# Revit family: Hager-VECTOR-Surface_mounted-IP65-With_Cover-With_DIN-NoHosted-CH-de
name_source: partatom
category: Electrical Equipment
units: mm (PartAtom-declared; Revit-internal decimal feet)

## family parameters
Always vertical = Yes
Cut with Voids When Loaded = No
Maintain Annotation Orientation = No
Panel Configuration = Two Columns, Circuits Across
Part Type = Panelboard
Room Calculation Point = No
Round Connector Dimension = Use Diameter
Shared = No
Work Plane-Based = Yes

## types (30) — shared parameters
Code hager = ADD-EC000214_EU
Default Elevation = 1200 mm
EF000003 - Montageart = Aufputz
EF000007 - Farbe = grau
EF000024 - UV-beständig = No
EF000116 - RAL-Nummer = 7035
EF000118 - Mit Montageplatte = No
EF001062 - EMV-Ausführung = No
EF001088 - Anbaumöglichkeit = Yes
EF001134 - DIN-Schiene = Yes
EF004462 - Art der Schließung = sonstige
EF005474 - Schutzart (IP) = IP65
EF006244 - Transparenter Deckel/Tür = Yes
EF006306 - Mit Schloss = No
EF015941 - Signaldurchlassende Tür = Yes
ETIM class code = EC000214
ETIM class name = Small distribution board
HG000001-Anzahl der Spalten = 1
HG000002-Mit tür = Yes
HG000003-Bereich = VECTOR
HG000005-Dicke = 2 mm  [stored 0.00656168 ft]
HG000006-Flush mounted = No
HG000009-Doppelflügeligen Tür = No
HG000010-Asymmetrische Türen = No
HG000011-Leere Reihen von unten = No
HG000012-Türschwenkwinkel = 90.00°
HG000013-Tür links = No
HG000014-Tür rechts = Yes
HG000015-Sichtbarkeit der Türöffnung = Yes
HG000016-3D-Türsichtbarkeit = Yes
HG000017-Distanz zwischen den Polen = 18 mm  [stored 0.0590551 ft]
HG000060-RAL-number = 7035
HG000099-Onfly Template ID-de-DE = 507532
Manufacturer = Hager
Name BIM&CO = Electricity
Name hager = ADD_Enclosures_EC000214
Reference = Template-Enclosure_EU-EC000214
Uniformat = Low Tension Service & Dist.
Uniformat code = D501001
zero-valued in all types: EF000218 - Einbautiefe, EF000332 - Einbauhöhe, EF000846 - Einbaubreite, EF001131 - Innentiefe, HG000007-Anzahl der leeren Spalten, HG000008-Anzahl der leeren Reihen

## per-type parameters (varying)
| type | BC_METADATA | EF000008 - Breite | EF000040 - Höhe | EF000049 - Tiefe | EF000266 - Anzahl der Reihen | EF002950 - Breite in Teilungseinheiten | EF009212 - Ausführung Deckel | EF015776 - Erdungsklemmenblock | EF015777 - Neutralleiterklemmenblock | HG000004-Herstellerreferenz | HGEF000266-Anzahl der Reihen | HGEF0002950-Breite in Teilungseinheiten |
| VECTOR-Surface_mounted_W111_H175_D93_3_Modular_Spacing-VE103A | {"ObjectGuid":"d3c7cbe9-06a7-4916-a6f3-f6102e421bbc","ModelGuid":"fb386d16-bb01-46b0-871a-5d369bb861f8","VariantGuid":"69505e22-49fc-412b-8c65-e0a7629c260b","Revision":"#30","VariantName":"VECTOR-Surface_mounted_W111_H175_D93_3_Modular_Spacing-VE103A"} | 111 mm | 175 mm  [stored 0.574147 ft] | 93 mm  [stored 0.305118 ft] | 1 | 3 | geschlossen | Yes | No | VE103A | 1 | 3 |
| VECTOR-Surface_mounted_W111_H175_D93_3_Modular_Spacing-VE103PN | {"ObjectGuid":"d3c7cbe9-06a7-4916-a6f3-f6102e421bbc","ModelGuid":"fb386d16-bb01-46b0-871a-5d369bb861f8","VariantGuid":"5bf82279-769e-45e9-843e-734a2e8b04b2","Revision":"#30","VariantName":"VECTOR-Surface_mounted_W111_H175_D93_3_Modular_Spacing-VE103PN"} | 111 mm | 175 mm  [stored 0.574147 ft] | 93 mm  [stored 0.305118 ft] | 1 | 3 | mit Ausschnitt | No | No | VE103PN | 1 | 3 |
| VECTOR-Surface_mounted_W111_H175_D93_3_Modular_Spacing-VE103SN | {"ObjectGuid":"d3c7cbe9-06a7-4916-a6f3-f6102e421bbc","ModelGuid":"fb386d16-bb01-46b0-871a-5d369bb861f8","VariantGuid":"e7d898c2-087d-478f-bfbd-9c783f3fbaf0","Revision":"#30","VariantName":"VECTOR-Surface_mounted_W111_H175_D93_3_Modular_Spacing-VE103SN"} | 111 mm | 175 mm  [stored 0.574147 ft] | 93 mm  [stored 0.305118 ft] | 1 | 3 | mit Ausschnitt | No | No | VE103SN | 1 | 3 |
| VECTOR-Surface_mounted_W165_H190_D113_6_Modular_Spacing-VE106A | {"ObjectGuid":"d3c7cbe9-06a7-4916-a6f3-f6102e421bbc","ModelGuid":"fb386d16-bb01-46b0-871a-5d369bb861f8","VariantGuid":"e3f62185-71a5-4f86-a256-2cf27b2b70b2","Revision":"#30","VariantName":"VECTOR-Surface_mounted_W165_H190_D113_6_Modular_Spacing-VE106A"} | 165 mm | 190 mm | 113 mm  [stored 0.370735 ft] | 1 | 6 | geschlossen | Yes | No | VE106A | 1 | 6 |
| VECTOR-Surface_mounted_W165_H190_D113_6_Modular_Spacing-VE106PN | {"ObjectGuid":"d3c7cbe9-06a7-4916-a6f3-f6102e421bbc","ModelGuid":"fb386d16-bb01-46b0-871a-5d369bb861f8","VariantGuid":"76445b86-cd2d-4a67-a9fa-ffff4e2ed3c8","Revision":"#30","VariantName":"VECTOR-Surface_mounted_W165_H190_D113_6_Modular_Spacing-VE106PN"} | 165 mm | 190 mm | 113 mm  [stored 0.370735 ft] | 1 | 6 | geschlossen | No | No | VE106PN | 1 | 6 |
| VECTOR-Surface_mounted_W165_H190_D113_6_Modular_Spacing-VE106SN | {"ObjectGuid":"d3c7cbe9-06a7-4916-a6f3-f6102e421bbc","ModelGuid":"fb386d16-bb01-46b0-871a-5d369bb861f8","VariantGuid":"b0e8016f-7a6b-4585-a6ec-a9ff9729da40","Revision":"#30","VariantName":"VECTOR-Surface_mounted_W165_H190_D113_6_Modular_Spacing-VE106SN"} | 165 mm | 190 mm | 113 mm  [stored 0.370735 ft] | 1 | 6 | mit Ausschnitt | No | No | VE106SN | 1 | 6 |
| VECTOR-Surface_mounted_W237_H210_D114_10_Modular_Spacing-VE110A | {"ObjectGuid":"d3c7cbe9-06a7-4916-a6f3-f6102e421bbc","ModelGuid":"fb386d16-bb01-46b0-871a-5d369bb861f8","VariantGuid":"4d85095b-6905-44da-a693-27a8f614f5e6","Revision":"#30","VariantName":"VECTOR-Surface_mounted_W237_H210_D114_10_Modular_Spacing-VE110A"} | 237 mm  [stored 0.777559 ft] | 210 mm  [stored 0.688976 ft] | 114 mm  [stored 0.374016 ft] | 1 | 10 | geschlossen | Yes | No | VE110A | 1 | 10 |
| VECTOR-Surface_mounted_W237_H210_D114_10_Modular_Spacing-VE110PN | {"ObjectGuid":"d3c7cbe9-06a7-4916-a6f3-f6102e421bbc","ModelGuid":"fb386d16-bb01-46b0-871a-5d369bb861f8","VariantGuid":"8b8af41c-55d3-4f54-a48d-69fb1ebbe829","Revision":"#30","VariantName":"VECTOR-Surface_mounted_W237_H210_D114_10_Modular_Spacing-VE110PN"} | 237 mm  [stored 0.777559 ft] | 210 mm  [stored 0.688976 ft] | 114 mm  [stored 0.374016 ft] | 1 | 10 | geschlossen | No | No | VE110PN | 1 | 10 |
| VECTOR-Surface_mounted_W237_H210_D114_10_Modular_Spacing-VE110SN | {"ObjectGuid":"d3c7cbe9-06a7-4916-a6f3-f6102e421bbc","ModelGuid":"fb386d16-bb01-46b0-871a-5d369bb861f8","VariantGuid":"02d3d4a0-a31d-4200-83ef-eeb133a9bbc4","Revision":"#30","VariantName":"VECTOR-Surface_mounted_W237_H210_D114_10_Modular_Spacing-VE110SN"} | 237 mm  [stored 0.777559 ft] | 210 mm  [stored 0.688976 ft] | 114 mm  [stored 0.374016 ft] | 1 | 10 | geschlossen | No | No | VE110SN | 1 | 10 |
| VECTOR-Surface_mounted_W310_H302_D151_12_Modular_Spacing-VE112AK | {"ObjectGuid":"d3c7cbe9-06a7-4916-a6f3-f6102e421bbc","ModelGuid":"fb386d16-bb01-46b0-871a-5d369bb861f8","VariantGuid":"d57e2aae-6186-4f79-9daa-0f27d3ef683b","Revision":"#30","VariantName":"VECTOR-Surface_mounted_W310_H302_D151_12_Modular_Spacing-VE112AK"} | 310 mm  [stored 1.01706 ft] | 302 mm  [stored 0.990814 ft] | 151 mm  [stored 0.495407 ft] | 1 | 12 | geschlossen | Yes | Yes | VE112AK | 1 | 12 |
| VECTOR-Surface_mounted_W310_H302_D151_12_Modular_Spacing-VE112PN | {"ObjectGuid":"d3c7cbe9-06a7-4916-a6f3-f6102e421bbc","ModelGuid":"fb386d16-bb01-46b0-871a-5d369bb861f8","VariantGuid":"1bbf5467-8e35-420d-9748-48cfdb1c49db","Revision":"#30","VariantName":"VECTOR-Surface_mounted_W310_H302_D151_12_Modular_Spacing-VE112PN"} | 310 mm  [stored 1.01706 ft] | 302 mm  [stored 0.990814 ft] | 151 mm  [stored 0.495407 ft] | 1 | 12 | geschlossen | No | No | VE112PN | 1 | 12 |
| VECTOR-Surface_mounted_W310_H302_D151_12_Modular_Spacing-VE112SN | {"ObjectGuid":"d3c7cbe9-06a7-4916-a6f3-f6102e421bbc","ModelGuid":"fb386d16-bb01-46b0-871a-5d369bb861f8","VariantGuid":"2669eab4-d3bd-4278-87ef-f939ce0a811b","Revision":"#30","VariantName":"VECTOR-Surface_mounted_W310_H302_D151_12_Modular_Spacing-VE112SN"} | 310 mm  [stored 1.01706 ft] | 302 mm  [stored 0.990814 ft] | 151 mm  [stored 0.495407 ft] | 1 | 12 | geschlossen | No | No | VE112SN | 1 | 12 |
| VECTOR-Surface_mounted_W418_H302_D151_18_Modular_Spacing-VE118AK | {"ObjectGuid":"d3c7cbe9-06a7-4916-a6f3-f6102e421bbc","ModelGuid":"fb386d16-bb01-46b0-871a-5d369bb861f8","VariantGuid":"f4e0934a-e4f0-446a-89c8-3abac548046a","Revision":"#30","VariantName":"VECTOR-Surface_mounted_W418_H302_D151_18_Modular_Spacing-VE118AK"} | 418 mm  [stored 1.37139 ft] | 302 mm  [stored 0.990814 ft] | 151 mm  [stored 0.495407 ft] | 1 | 18 | geschlossen | Yes | Yes | VE118AK | 1 | 18 |
| VECTOR-Surface_mounted_W418_H302_D151_18_Modular_Spacing-VE118PN | {"ObjectGuid":"d3c7cbe9-06a7-4916-a6f3-f6102e421bbc","ModelGuid":"fb386d16-bb01-46b0-871a-5d369bb861f8","VariantGuid":"06ed9296-9994-441a-a687-3948c0a79dd1","Revision":"#30","VariantName":"VECTOR-Surface_mounted_W418_H302_D151_18_Modular_Spacing-VE118PN"} | 418 mm  [stored 1.37139 ft] | 302 mm  [stored 0.990814 ft] | 151 mm  [stored 0.495407 ft] | 1 | 18 | geschlossen | No | No | VE118PN | 1 | 18 |
| VECTOR-Surface_mounted_W418_H302_D151_18_Modular_Spacing-VE118SN | {"ObjectGuid":"d3c7cbe9-06a7-4916-a6f3-f6102e421bbc","ModelGuid":"fb386d16-bb01-46b0-871a-5d369bb861f8","VariantGuid":"4a2194d9-89a4-4a4b-ac45-6e89e3566a8e","Revision":"#30","VariantName":"VECTOR-Surface_mounted_W418_H302_D151_18_Modular_Spacing-VE118SN"} | 418 mm  [stored 1.37139 ft] | 302 mm  [stored 0.990814 ft] | 151 mm  [stored 0.495407 ft] | 1 | 18 | geschlossen | No | No | VE118SN | 1 | 18 |
| VECTOR-Surface_mounted_W310_H427_D151_12_Modular_Spacing-VE212AK | {"ObjectGuid":"d3c7cbe9-06a7-4916-a6f3-f6102e421bbc","ModelGuid":"fb386d16-bb01-46b0-871a-5d369bb861f8","VariantGuid":"c01b0445-b96e-4ca0-8f36-f3b77660627c","Revision":"#30","VariantName":"VECTOR-Surface_mounted_W310_H427_D151_12_Modular_Spacing-VE212AK"} | 310 mm  [stored 1.01706 ft] | 427 mm  [stored 1.40092 ft] | 151 mm  [stored 0.495407 ft] | 2 | 12 | geschlossen | Yes | Yes | VE212AK | 2 | 12 |
| VECTOR-Surface_mounted_W310_H427_D151_12_Modular_Spacing-VE212PN | {"ObjectGuid":"d3c7cbe9-06a7-4916-a6f3-f6102e421bbc","ModelGuid":"fb386d16-bb01-46b0-871a-5d369bb861f8","VariantGuid":"29390155-c559-412c-8a29-67b206487e47","Revision":"#30","VariantName":"VECTOR-Surface_mounted_W310_H427_D151_12_Modular_Spacing-VE212PN"} | 310 mm  [stored 1.01706 ft] | 427 mm  [stored 1.40092 ft] | 151 mm  [stored 0.495407 ft] | 2 | 12 | geschlossen | No | No | VE212PN | 2 | 12 |
| VECTOR-Surface_mounted_W310_H427_D151_12_Modular_Spacing-VE212SN | {"ObjectGuid":"d3c7cbe9-06a7-4916-a6f3-f6102e421bbc","ModelGuid":"fb386d16-bb01-46b0-871a-5d369bb861f8","VariantGuid":"e55af2bb-5e56-47f6-8731-15f48f08de25","Revision":"#30","VariantName":"VECTOR-Surface_mounted_W310_H427_D151_12_Modular_Spacing-VE212SN"} | 310 mm  [stored 1.01706 ft] | 427 mm  [stored 1.40092 ft] | 151 mm  [stored 0.495407 ft] | 2 | 12 | geschlossen | No | No | VE212SN | 2 | 12 |
| VECTOR-Surface_mounted_W418_H452_D151_18_Modular_Spacing-VE218AK | {"ObjectGuid":"d3c7cbe9-06a7-4916-a6f3-f6102e421bbc","ModelGuid":"fb386d16-bb01-46b0-871a-5d369bb861f8","VariantGuid":"071168f8-5f04-42d3-9594-f27b45a714b0","Revision":"#30","VariantName":"VECTOR-Surface_mounted_W418_H452_D151_18_Modular_Spacing-VE218AK"} | 418 mm  [stored 1.37139 ft] | 452 mm  [stored 1.48294 ft] | 151 mm  [stored 0.495407 ft] | 2 | 18 | geschlossen | Yes | Yes | VE218AK | 2 | 18 |
| VECTOR-Surface_mounted_W418_H452_D151_18_Modular_Spacing-VE218PN | {"ObjectGuid":"d3c7cbe9-06a7-4916-a6f3-f6102e421bbc","ModelGuid":"fb386d16-bb01-46b0-871a-5d369bb861f8","VariantGuid":"0d35b193-4191-4109-bc17-61772ba32f38","Revision":"#30","VariantName":"VECTOR-Surface_mounted_W418_H452_D151_18_Modular_Spacing-VE218PN"} | 418 mm  [stored 1.37139 ft] | 452 mm  [stored 1.48294 ft] | 151 mm  [stored 0.495407 ft] | 2 | 18 | geschlossen | No | No | VE218PN | 2 | 18 |
| VECTOR-Surface_mounted_W418_H452_D151_18_Modular_Spacing-VE218SN | {"ObjectGuid":"d3c7cbe9-06a7-4916-a6f3-f6102e421bbc","ModelGuid":"fb386d16-bb01-46b0-871a-5d369bb861f8","VariantGuid":"5ce8ec51-292b-4520-aedd-a2f68059377e","Revision":"#30","VariantName":"VECTOR-Surface_mounted_W418_H452_D151_18_Modular_Spacing-VE218SN"} | 418 mm  [stored 1.37139 ft] | 452 mm  [stored 1.48294 ft] | 151 mm  [stored 0.495407 ft] | 2 | 18 | mit Ausschnitt | No | No | VE218SN | 2 | 18 |
| VECTOR-Surface_mounted_W310_H552_D151_12_Modular_Spacing-VE312AK | {"ObjectGuid":"d3c7cbe9-06a7-4916-a6f3-f6102e421bbc","ModelGuid":"fb386d16-bb01-46b0-871a-5d369bb861f8","VariantGuid":"985dcad2-cb6b-48e4-a831-58c3bf16bc09","Revision":"#30","VariantName":"VECTOR-Surface_mounted_W310_H552_D151_12_Modular_Spacing-VE312AK"} | 310 mm  [stored 1.01706 ft] | 552 mm  [stored 1.81102 ft] | 151 mm  [stored 0.495407 ft] | 3 | 12 | geschlossen | Yes | Yes | VE312AK | 3 | 12 |
| VECTOR-Surface_mounted_W310_H552_D151_12_Modular_Spacing-VE312PN | {"ObjectGuid":"d3c7cbe9-06a7-4916-a6f3-f6102e421bbc","ModelGuid":"fb386d16-bb01-46b0-871a-5d369bb861f8","VariantGuid":"5fd972b5-eb19-4fd5-8bc7-0ea5c1995523","Revision":"#30","VariantName":"VECTOR-Surface_mounted_W310_H552_D151_12_Modular_Spacing-VE312PN"} | 310 mm  [stored 1.01706 ft] | 552 mm  [stored 1.81102 ft] | 151 mm  [stored 0.495407 ft] | 3 | 12 | geschlossen | No | No | VE312PN | 3 | 12 |
| VECTOR-Surface_mounted_W310_H552_D151_12_Modular_Spacing-VE312SN | {"ObjectGuid":"d3c7cbe9-06a7-4916-a6f3-f6102e421bbc","ModelGuid":"fb386d16-bb01-46b0-871a-5d369bb861f8","VariantGuid":"0b169c55-73aa-49fa-a256-de3d5b87279f","Revision":"#30","VariantName":"VECTOR-Surface_mounted_W310_H552_D151_12_Modular_Spacing-VE312SN"} | 310 mm  [stored 1.01706 ft] | 552 mm  [stored 1.81102 ft] | 151 mm  [stored 0.495407 ft] | 3 | 12 | mit Ausschnitt | No | No | VE312SN | 3 | 12 |
| VECTOR-Surface_mounted_W418_H602_D151_18_Modular_Spacing-VE318AK | {"ObjectGuid":"d3c7cbe9-06a7-4916-a6f3-f6102e421bbc","ModelGuid":"fb386d16-bb01-46b0-871a-5d369bb861f8","VariantGuid":"f59808b9-94ed-4f9a-a9f3-fad96712e3d5","Revision":"#30","VariantName":"VECTOR-Surface_mounted_W418_H602_D151_18_Modular_Spacing-VE318AK"} | 418 mm  [stored 1.37139 ft] | 602 mm  [stored 1.97507 ft] | 151 mm  [stored 0.495407 ft] | 3 | 18 | geschlossen | Yes | Yes | VE318AK | 3 | 18 |
| VECTOR-Surface_mounted_W418_H602_D151_18_Modular_Spacing-VE318PN | {"ObjectGuid":"d3c7cbe9-06a7-4916-a6f3-f6102e421bbc","ModelGuid":"fb386d16-bb01-46b0-871a-5d369bb861f8","VariantGuid":"898ef6bb-c339-4143-ac22-058a11371116","Revision":"#30","VariantName":"VECTOR-Surface_mounted_W418_H602_D151_18_Modular_Spacing-VE318PN"} | 418 mm  [stored 1.37139 ft] | 602 mm  [stored 1.97507 ft] | 151 mm  [stored 0.495407 ft] | 3 | 18 | geschlossen | No | No | VE318PN | 3 | 18 |
| VECTOR-Surface_mounted_W418_H602_D151_18_Modular_Spacing-VE318SN | {"ObjectGuid":"d3c7cbe9-06a7-4916-a6f3-f6102e421bbc","ModelGuid":"fb386d16-bb01-46b0-871a-5d369bb861f8","VariantGuid":"b447e2ed-7aed-4123-8ac3-e468ff640952","Revision":"#30","VariantName":"VECTOR-Surface_mounted_W418_H602_D151_18_Modular_Spacing-VE318SN"} | 418 mm  [stored 1.37139 ft] | 602 mm  [stored 1.97507 ft] | 151 mm  [stored 0.495407 ft] | 3 | 18 | mit Ausschnitt | No | No | VE318SN | 3 | 18 |
| VECTOR-Surface_mounted_W310_H677_D151_12_Modular_Spacing-VE412AK | {"ObjectGuid":"d3c7cbe9-06a7-4916-a6f3-f6102e421bbc","ModelGuid":"fb386d16-bb01-46b0-871a-5d369bb861f8","VariantGuid":"74f10b49-5141-44f1-9064-345dd258739c","Revision":"#30","VariantName":"VECTOR-Surface_mounted_W310_H677_D151_12_Modular_Spacing-VE412AK"} | 310 mm  [stored 1.01706 ft] | 677 mm  [stored 2.22113 ft] | 151 mm  [stored 0.495407 ft] | 4 | 12 | geschlossen | Yes | Yes | VE412AK | 4 | 12 |
| VECTOR-Surface_mounted_W310_H677_D151_12_Modular_Spacing-VE412PN | {"ObjectGuid":"d3c7cbe9-06a7-4916-a6f3-f6102e421bbc","ModelGuid":"fb386d16-bb01-46b0-871a-5d369bb861f8","VariantGuid":"98263da4-9922-4341-87c6-e22d3c299bf5","Revision":"#30","VariantName":"VECTOR-Surface_mounted_W310_H677_D151_12_Modular_Spacing-VE412PN"} | 310 mm  [stored 1.01706 ft] | 677 mm  [stored 2.22113 ft] | 151 mm  [stored 0.495407 ft] | 4 | 12 | geschlossen | No | No | VE412PN | 4 | 12 |
| VECTOR-Surface_mounted_W310_H677_D151_12_Modular_Spacing-VE412SN | {"ObjectGuid":"d3c7cbe9-06a7-4916-a6f3-f6102e421bbc","ModelGuid":"fb386d16-bb01-46b0-871a-5d369bb861f8","VariantGuid":"449511b3-7730-4b20-9492-a461bbaa7097","Revision":"#30","VariantName":"VECTOR-Surface_mounted_W310_H677_D151_12_Modular_Spacing-VE412SN"} | 310 mm  [stored 1.01706 ft] | 677 mm  [stored 2.22113 ft] | 151 mm  [stored 0.495407 ft] | 4 | 12 | mit Ausschnitt | No | No | VE412SN | 4 | 12 |

note: [stored X ft] marks values corroborated as IEEE doubles in the binary element streams (Revit-internal decimal feet)

## geometry (parser evidence)
native form markers: Sweep x14
no freeform markers — native parametric forms only
